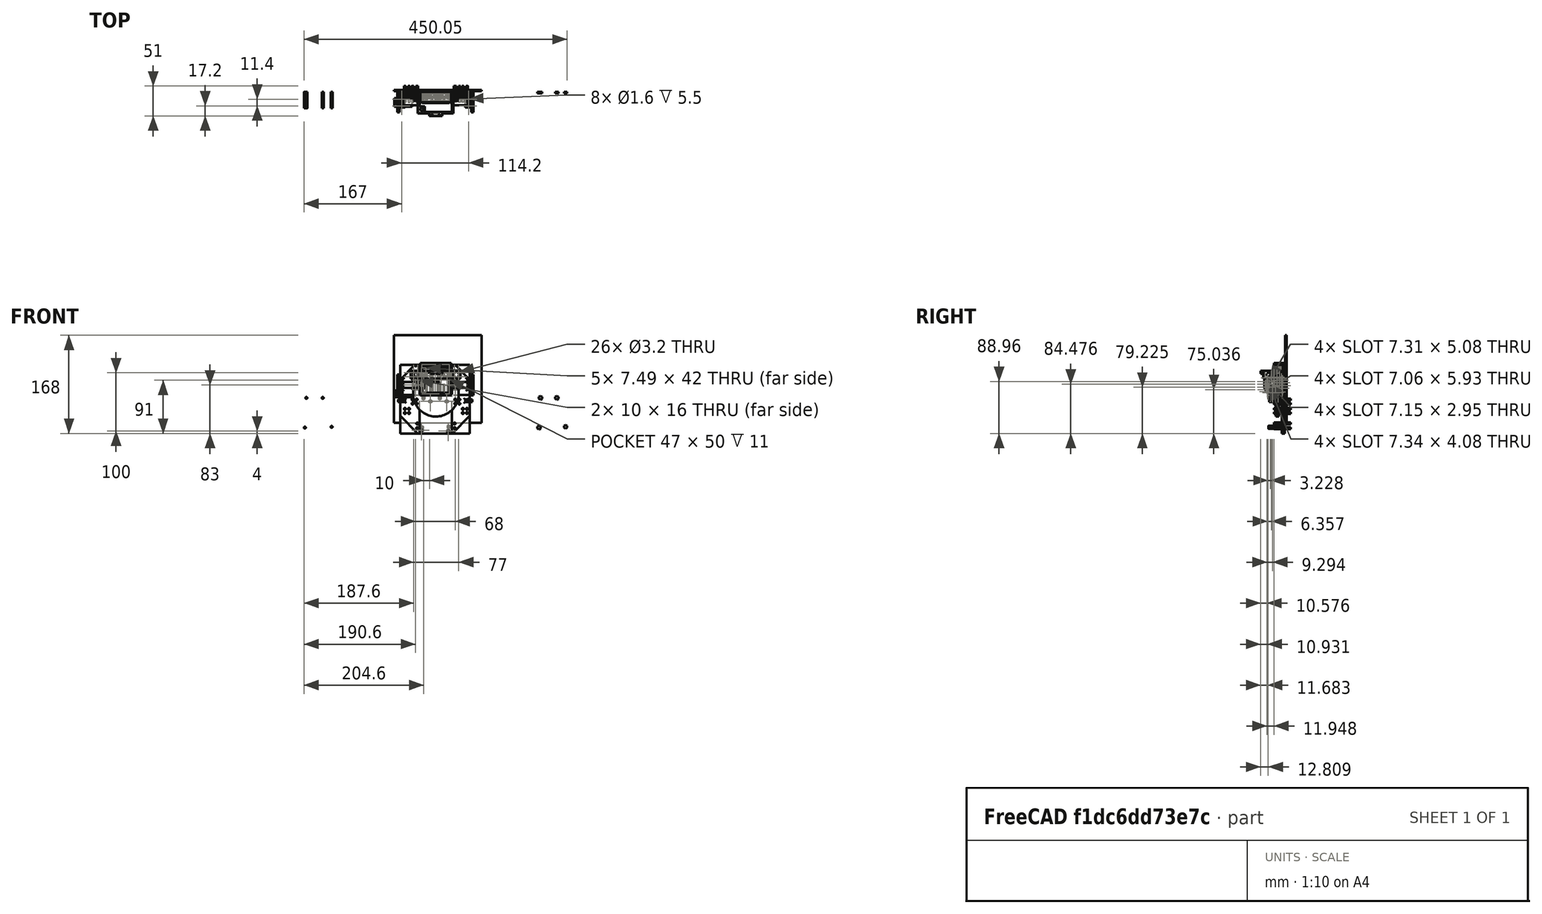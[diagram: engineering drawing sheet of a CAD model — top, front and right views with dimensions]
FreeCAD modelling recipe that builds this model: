
FCSTD DOCUMENT  (FreeCAD 0.16R6712 (Git))
Label: 5028.3 Frank the Robot
License: All rights reserved
LicenseURL: http://en.wikipedia.org/wiki/All_rights_reserved
objects: Part::Cylinder×87, Part::Cut×49, Part::Fuse×46, Part::Box×45, Part::MultiFuse×20, Part::Feature×17, Part::Fillet×10, Part::Mirroring×8, Part::Chamfer×7, Part::Cone×4, Part::Compound×3, Part::Torus×2, App::DocumentObjectGroup×1
note: 298 computed .brp shape members not serialized (recipe doc carries the construction recipe); baked Part::Feature solids carry a one-line shape summary decoded from their .brp

FEATURE [Part::Cylinder] Cylinder
  Angle = 360
  Height = 30
  Radius = 7
FEATURE [Part::Cylinder] Cylinder001
  Angle = 360
  Height = 19
  Placement = pos=(0,0,30) rot=(0,0,1;0rad)
  Radius = 7
FEATURE [Part::Cylinder] Cylinder002
  Angle = 360
  Height = 1.8
  Placement = pos=(0,0,49) rot=(0,0,1;0rad)
  Radius = 2.5
FEATURE [Part::Compound] Compound
  Links = -> [Cylinder,Cylinder002,Cylinder001]
FEATURE [Part::Cylinder] Cylinder003
  Angle = 360
  Height = 30
  Radius = 7
FEATURE [Part::Cylinder] Cylinder004
  Angle = 360
  Height = 19
  Placement = pos=(0,0,30) rot=(0,0,1;0rad)
  Radius = 7
FEATURE [Part::Cylinder] Cylinder005
  Angle = 360
  Height = 1.8
  Placement = pos=(0,0,49) rot=(0,0,1;0rad)
  Radius = 2.5
FEATURE [Part::Compound] Compound001
  Links = -> [Cylinder003,Cylinder005,Cylinder004]
  Placement = pos=(14.5,0,50) rot=(1,0,0;3.14159rad)
FEATURE [Part::Cylinder] Cylinder006
  Angle = 360
  Height = 30
  Radius = 7
FEATURE [Part::Cylinder] Cylinder007
  Angle = 360
  Height = 19
  Placement = pos=(0,0,30) rot=(0,0,1;0rad)
  Radius = 7
FEATURE [Part::Cylinder] Cylinder008
  Angle = 360
  Height = 1.8
  Placement = pos=(0,0,49) rot=(0,0,1;0rad)
  Radius = 2.5
FEATURE [Part::Compound] Compound002
  Links = -> [Cylinder006,Cylinder008,Cylinder007]
  Placement = pos=(29,0,0) rot=(0,0,1;0rad)
FEATURE [Part::Box] Box  label="Cube"
  Height = 50
  Length = 47
  Placement = pos=(-9,-8,0) rot=(0,0,1;0rad)
  Width = 12
FEATURE [Part::Box] Box001  label="Cube001"
  Height = 55
  Length = 53
  Placement = pos=(-12,-8,-2.5) rot=(0,0,1;0rad)
  Width = 11
FEATURE [Part::Cylinder] Cylinder009
  Angle = 360
  Height = 50
  Radius = 7
FEATURE [Part::Cylinder] Cylinder010
  Angle = 360
  Height = 50
  Placement = pos=(14.5,0,0) rot=(0,0,1;0rad)
  Radius = 7
FEATURE [Part::Cut] Cut
  Base = -> Box001
  Tool = -> Box
FEATURE [Part::Box] Box002  label="Cube002"
  Height = 55
  Length = 53
  Placement = pos=(-12,3,-2.5) rot=(0,0,1;0rad)
  Width = 7
FEATURE [Part::Fuse] Fusion
  Base = -> Cut
  Tool = -> Box002
FEATURE [Part::Cut] Cut001  label="No idea why this is here...."
  Base = -> Fusion
  Tool = -> Cylinder009
FEATURE [Part::Cylinder] Cylinder011
  Angle = 360
  Height = 50
  Placement = pos=(29,0,0) rot=(0,0,1;0rad)
  Radius = 7
FEATURE [Part::Box] Box003  label="Cube003"
  Height = 5
  Length = 2
  Placement = pos=(28,-9,-2) rot=(0,0,1;0rad)
  Width = 12
FEATURE [Part::Box] Box004  label="Cube004"
  Height = 5
  Length = 2
  Placement = pos=(18.5,-9,46) rot=(0,0,1;0rad)
  Width = 12
FEATURE [Part::Box] Box005  label="Cube005"
  Height = 5
  Length = 2
  Placement = pos=(-2,-9,46) rot=(0,0,1;0rad)
  Width = 12
FEATURE [Part::Box] Box006  label="Cube006"
  Height = 5
  Length = 3
  Placement = pos=(35,-9,-4) rot=(0,0,1;0rad)
  Width = 12
FEATURE [Part::Cut] Cut008
FEATURE [Part::Torus] Torus001
  Angle1 = -180
  Angle2 = 180
  Angle3 = 360
  Placement = pos=(0,0,2) rot=(0,0,1;0rad)
  Radius1 = 19
  Radius2 = 1.5
FEATURE [Part::Cut] Cut009  label="wheel2"
  Base = -> Cut008
  Placement = pos=(75,-7,15) rot=(0,1,0;1.5708rad)
  Tool = -> Torus001
FEATURE [Part::Torus] Torus
  Angle1 = -180
  Angle2 = 180
  Angle3 = 360
  Placement = pos=(0,0,2) rot=(0,0,1;0rad)
  Radius1 = 19
  Radius2 = 1.5
FEATURE [Part::Cut] Cut010
FEATURE [Part::Cut] Cut011  label="wheel1"
  Base = -> Cut010
  Placement = pos=(-51,-7,15) rot=(0,1,0;1.5708rad)
  Tool = -> Torus
FEATURE [Part::Fuse] Fusion003
FEATURE [Part::Cylinder] Cylinder012
  Angle = 360
  Height = 10
  Placement = pos=(5,-4.5,0) rot=(0,1,0;1.5708rad)
  Radius = 0.8
FEATURE [Part::Fuse] Fusion048  label="right-motor001"
  Base = -> Cylinder012
  Placement = pos=(-51,-7,15) rot=(0,0,1;0rad)
  Tool = -> Fusion003
FEATURE [Part::Fuse] Fusion049
FEATURE [Part::Cylinder] Cylinder013
  Angle = 360
  Height = 10
  Placement = pos=(5,-4.5,0) rot=(0,1,0;1.5708rad)
  Radius = 0.8
FEATURE [Part::Fuse] Fusion050  label="left-motor001"
  Base = -> Cylinder013
  Placement = pos=(79,-7,15) rot=(0,0,1;3.14159rad)
  Tool = -> Fusion049
FEATURE [Part::Box] Box007  label="Cube007"
  Height = 5
  Length = 2
  Placement = pos=(37.5,-9,46) rot=(0,0,1;0rad)
  Width = 12
FEATURE [Part::Box] Box008  label="Cube008"
  Height = 5
  Length = 2
  Placement = pos=(8,-9,-2) rot=(0,0,1;0rad)
  Width = 12
FEATURE [Part::Box] Box009  label="The Ground"
  Height = 150
  Length = 150
  Placement = pos=(-57,11,-50) rot=(0,0,1;0rad)
  Width = 2
FEATURE [Part::Box] Box010  label="Motor Mount Left"
  Height = 16
  Length = 4
  Placement = pos=(69,-13,7) rot=(0,0,1;0rad)
  Width = 20
FEATURE [Part::Box] Box011  label="Motor Mount Right"
  Height = 16
  Length = 4
  Placement = pos=(-46,-13,7) rot=(0,0,1;0rad)
  Width = 20
FEATURE [Part::Box] Box012  label="Motor Support Right"
  Height = 16
  Length = 10
  Placement = pos=(-25,-1,7) rot=(0,0,1;0rad)
  Width = 8
FEATURE [Part::Box] Box013  label="Motor Support Left"
  Height = 16
  Length = 10
  Placement = pos=(43,-1,7) rot=(0,0,1;0rad)
  Width = 8
FEATURE [Part::Cylinder] Cylinder014
  Angle = 360
  Height = 28
  Placement = pos=(40.7,0,-10.3) rot=(1,0,0;1.5708rad)
  Radius = 1.6
FEATURE [Part::Cylinder] Cylinder015
  Angle = 360
  Height = 28
  Placement = pos=(-2.4,0,-59.8) rot=(1,0,0;1.5708rad)
  Radius = 1.6
FEATURE [Part::Cylinder] Cylinder016
  Angle = 360
  Height = 28
  Placement = pos=(-5,0,-9) rot=(1,0,0;1.5708rad)
  Radius = 1.6
FEATURE [Part::Cylinder] Cylinder017
  Angle = 360
  Height = 28
  Placement = pos=(25.5,0,-59.8) rot=(1,0,0;1.5708rad)
  Radius = 1.6
FEATURE [Part::Fuse] Fusion051
  Base = -> Cylinder015
  Tool = -> Cylinder016
FEATURE [Part::Fuse] Fusion052
  Base = -> Cylinder014
  Tool = -> Cylinder017
FEATURE [Part::Fuse] Fusion053  label="Screw holes on Arduino Duo"
  Base = -> Fusion051
  Tool = -> Fusion052
FEATURE [Part::Mirroring] Part__Mirroring  label="XXXXXScrew holes on Arduino Duo (Mirror #1)"
  Base = (0,0,0)
  Normal = (0,0,1)
  Placement = pos=(-204,10,-67) rot=(0,0,1;0rad)
  Source = -> Fusion053
FEATURE [Part::Box] Box014  label="Not used Cube"
  Height = 51
  Length = 119
  Placement = pos=(-46,7,-2) rot=(0,0,1;0rad)
  Width = 3
FEATURE [Part::Box] Box015  label="Cube014 Arduino Support cube"
  Height = 67
  Length = 55
  Placement = pos=(-13,5,-68) rot=(0,0,1;0rad)
  Width = 5
FEATURE [Part::Cylinder] Cylinder018
  Angle = 360
  Height = 5
  Placement = pos=(15,0,0) rot=(1,0,0;1.5708rad)
  Radius = 39
FEATURE [Part::Cut] Cut014  label="M3 Nut"
  Base = -> Cut001
  Placement = pos=(-6.4,10,-7.2) rot=(1,0,0;1.5708rad)
  Tool = -> Cylinder001
FEATURE [Part::Cut] Cut015  label="M3 Nut001"
  Base = -> Cut001
  Placement = pos=(21.5,10,-7.2) rot=(1,0,0;1.5708rad)
  Tool = -> Cylinder001
FEATURE [Part::Cut] Cut016  label="M3 Nut002"
  Base = -> Cut001
  Placement = pos=(36.7,10,-56.7) rot=(1,0,0;1.5708rad)
  Tool = -> Cylinder001
FEATURE [Part::Cut] Cut017  label="M3 Nut003"
  Base = -> Cut001
  Placement = pos=(-9,10,-58) rot=(1,0,0;1.5708rad)
  Tool = -> Cylinder001
FEATURE [Part::Cut] Cut018
  Base = -> Cut
  Placement = pos=(-9,10,-58) rot=(1,0,0;1.5708rad)
  Tool = -> Box006
FEATURE [Part::Cut] Cut019
  Base = -> Cut
  Placement = pos=(36.7,10,-56.7) rot=(1,0,0;1.5708rad)
  Tool = -> Box006
FEATURE [Part::Cut] Cut020
  Base = -> Cut
  Placement = pos=(-6.4,10,-7.2) rot=(1,0,0;1.5708rad)
  Tool = -> Box006
FEATURE [Part::Cut] Cut021
  Base = -> Cut
  Placement = pos=(21.5,10,-7.2) rot=(1,0,0;1.5708rad)
  Tool = -> Box006
FEATURE [Part::MultiFuse] Fusion054  label="XXXXXHex Holes"
  Placement = pos=(200,0,0) rot=(0,0,1;0rad)
  Shapes = -> [Cut018,Cut021,Cut019,Cut020]
FEATURE [Part::Box] Box016  label="Cube015"
  Height = 117
  Length = 33
  Placement = pos=(-46,7,-68) rot=(0,0,1;0rad)
  Width = 3
FEATURE [Part::Box] Box017  label="Cube016"
  Height = 117
  Length = 31
  Placement = pos=(42,7,-68) rot=(0,0,1;0rad)
  Width = 3
FEATURE [Part::Cylinder] Cylinder019
  Angle = 360
  Height = 28
  Placement = pos=(48,20,-10) rot=(1,0,0;1.5708rad)
  Radius = 1.6
FEATURE [Part::Cylinder] Cylinder020
  Angle = 360
  Height = 28
  Placement = pos=(47,20,-51) rot=(1,0,0;1.5708rad)
  Radius = 1.6
FEATURE [Part::Cylinder] Cylinder021
  Angle = 360
  Height = 28
  Placement = pos=(48,20,-17) rot=(1,0,0;1.5708rad)
  Radius = 1.6
FEATURE [Part::Cylinder] Cylinder022
  Angle = 360
  Height = 28
  Placement = pos=(47,20,-59) rot=(1,0,0;1.5708rad)
  Radius = 1.6
FEATURE [Part::Cylinder] Cylinder023
  Angle = 360
  Height = 28
  Placement = pos=(55,20,-17) rot=(1,0,0;1.5708rad)
  Radius = 1.6
FEATURE [Part::Cylinder] Cylinder024
  Angle = 360
  Height = 28
  Placement = pos=(55,20,-10) rot=(1,0,0;1.5708rad)
  Radius = 1.6
FEATURE [Part::MultiFuse] Fusion055
  Shapes = -> [Cylinder021,Cylinder023,Cylinder024,Cylinder019]
FEATURE [Part::MultiFuse] Fusion056
  Placement = pos=(13,0,-16) rot=(0,0,1;0rad)
  Shapes = -> [Cylinder021,Cylinder023,Cylinder024,Cylinder019]
FEATURE [Part::MultiFuse] Fusion057  label="Mount holes top left"
  Placement = pos=(-1,0,46) rot=(0,0,1;0rad)
  Shapes = -> [Cylinder021,Cylinder023,Cylinder024,Cylinder019]
FEATURE [Part::MultiFuse] Fusion058  label="Mount holes top right"
  Placement = pos=(-71,0,46) rot=(0,0,1;0rad)
  Shapes = -> [Cylinder021,Cylinder023,Cylinder024,Cylinder019]
FEATURE [Part::MultiFuse] Fusion059
  Shapes = -> [Cylinder022,Cylinder020,Fusion055,Fusion056]
FEATURE [Part::Mirroring] Part__Mirroring001  label="Mount holes bottom right"
  Base = (0,0,0)
  Normal = (1,0,0)
  Placement = pos=(30,0,0) rot=(0,0,1;0rad)
  Source = -> Fusion059
FEATURE [Part::Cylinder] Cylinder025
  Angle = 360
  Height = 28
  Placement = pos=(48,20,-10) rot=(1,0,0;1.5708rad)
  Radius = 1.6
FEATURE [Part::Cylinder] Cylinder026
  Angle = 360
  Height = 28
  Placement = pos=(47,20,-51) rot=(1,0,0;1.5708rad)
  Radius = 1.6
FEATURE [Part::Cylinder] Cylinder027
  Angle = 360
  Height = 28
  Placement = pos=(48,20,-17) rot=(1,0,0;1.5708rad)
  Radius = 1.6
FEATURE [Part::Cylinder] Cylinder028
  Angle = 360
  Height = 28
  Placement = pos=(47,20,-59) rot=(1,0,0;1.5708rad)
  Radius = 1.6
FEATURE [Part::Cylinder] Cylinder029
  Angle = 360
  Height = 28
  Placement = pos=(55,20,-17) rot=(1,0,0;1.5708rad)
  Radius = 1.6
FEATURE [Part::Cylinder] Cylinder030
  Angle = 360
  Height = 28
  Placement = pos=(55,20,-10) rot=(1,0,0;1.5708rad)
  Radius = 1.6
FEATURE [Part::MultiFuse] Fusion060
  Shapes = -> [Cylinder027,Cylinder029,Cylinder030,Cylinder025]
FEATURE [Part::MultiFuse] Fusion061
  Placement = pos=(13,0,-16) rot=(0,0,1;0rad)
  Shapes = -> [Cylinder027,Cylinder029,Cylinder030,Cylinder025]
FEATURE [Part::MultiFuse] Fusion062  label="Mount holes bottom left"
  Shapes = -> [Cylinder028,Cylinder026,Fusion060,Fusion061]
FEATURE [Part::Cylinder] Cylinder031  label="Cylinder087"
  Angle = 360
  Height = 10
  Placement = pos=(0,18,29) rot=(0,0,1;0rad)
  Radius = 2.25
FEATURE [Part::Cylinder] Cylinder032  label="Cylinder088"
  Angle = 360
  Height = 10
  Placement = pos=(4.5,18,32) rot=(0,0,1;0rad)
  Radius = 1
FEATURE [Part::Cylinder] Cylinder033  label="Cylinder089"
  Angle = 360
  Height = 10
  Placement = pos=(-4.5,18,32) rot=(0,0,1;0rad)
  Radius = 1
FEATURE [Part::Fuse] Fusion009  label="Mounting Screw Holes"
  Base = -> Cylinder032
  Tool = -> Cylinder033
FEATURE [Part::Fuse] Fusion071  label="Motor Holes Left"
  Base = -> Cylinder031
  Placement = pos=(37,-7,-3) rot=(0.57735,0.57735,0.57735;2.0944rad)
  Tool = -> Fusion009
FEATURE [Part::Cylinder] Cylinder034  label="Cylinder090"
  Angle = 360
  Height = 10
  Placement = pos=(0,18,29) rot=(0,0,1;0rad)
  Radius = 2.25
FEATURE [Part::Cylinder] Cylinder035  label="Cylinder091"
  Angle = 360
  Height = 10
  Placement = pos=(4.5,18,32) rot=(0,0,1;0rad)
  Radius = 1
FEATURE [Part::Cylinder] Cylinder036  label="Cylinder092"
  Angle = 360
  Height = 10
  Placement = pos=(-4.5,18,32) rot=(0,0,1;0rad)
  Radius = 1
FEATURE [Part::Fuse] Fusion072  label="Mounting Screw Holes001"
  Base = -> Cylinder035
  Tool = -> Cylinder036
FEATURE [Part::Fuse] Fusion073  label="Motor Holes Right"
  Base = -> Cylinder034
  Placement = pos=(-79,-7,-3) rot=(0.57735,0.57735,0.57735;2.0944rad)
  Tool = -> Fusion072
FEATURE [Part::Cylinder] Cylinder037  label="Cylinder093"
  Angle = 360
  Height = 28
  Placement = pos=(40.7,0,-10.3) rot=(1,0,0;1.5708rad)
  Radius = 1.6
FEATURE [Part::Cylinder] Cylinder038  label="Cylinder094"
  Angle = 360
  Height = 28
  Placement = pos=(-2.4,0,-59.8) rot=(1,0,0;1.5708rad)
  Radius = 1.6
FEATURE [Part::Cylinder] Cylinder039  label="Cylinder095"
  Angle = 360
  Height = 28
  Placement = pos=(-5,0,-9) rot=(1,0,0;1.5708rad)
  Radius = 1.6
FEATURE [Part::Cylinder] Cylinder040  label="Cylinder096"
  Angle = 360
  Height = 28
  Placement = pos=(25.5,0,-59.8) rot=(1,0,0;1.5708rad)
  Radius = 1.6
FEATURE [Part::Fuse] Fusion074
  Base = -> Cylinder038
  Tool = -> Cylinder039
FEATURE [Part::Fuse] Fusion075
  Base = -> Cylinder037
  Tool = -> Cylinder040
FEATURE [Part::Fuse] Fusion076  label="Screw holes on Arduino Duo001"
  Base = -> Fusion074
  Tool = -> Fusion075
FEATURE [Part::Mirroring] Part__Mirroring002  label="Screw holes on Arduino Duo (Mirror #1)001"
  Base = (0,0,0)
  Normal = (0,0,1)
  Placement = pos=(-4,10,-67) rot=(0,0,1;0rad)
  Source = -> Fusion076
FEATURE [Part::Mirroring] Part__Mirroring003  label="Screw holes on Arduino Duo (Mirror #1)001 (Mirror #4)"
  Base = (0,0,0)
  Normal = (1,0,0)
  Placement = pos=(27,0,-6) rot=(0,0,1;0rad)
  Source = -> Part__Mirroring002
FEATURE [Part::Box] Box018  label="Cube017"
  Height = 50
  Length = 47
  Placement = pos=(-9,-8,0) rot=(0,0,1;0rad)
  Width = 12
FEATURE [Part::Box] Box019  label="Cube018"
  Height = 55
  Length = 53
  Placement = pos=(-12,-8,-2.5) rot=(0,0,1;0rad)
  Width = 11
FEATURE [Part::Cut] Cut031
  Base = -> Box019
  Tool = -> Box018
FEATURE [Part::Box] Box020  label="Cube019"
  Height = 5
  Length = 3
  Placement = pos=(35,-9,-4) rot=(0,0,1;0rad)
  Width = 12
FEATURE [Part::Cut] Cut032
  Base = -> Cut031
  Placement = pos=(-9,10,-58) rot=(1,0,0;1.5708rad)
  Tool = -> Box020
FEATURE [Part::Cut] Cut033
  Base = -> Cut031
  Placement = pos=(36.7,10,-56.7) rot=(1,0,0;1.5708rad)
  Tool = -> Box020
FEATURE [Part::Cut] Cut034
  Base = -> Cut031
  Placement = pos=(-6.4,10,-7.2) rot=(1,0,0;1.5708rad)
  Tool = -> Box020
FEATURE [Part::Cut] Cut035
  Base = -> Cut031
  Placement = pos=(21.5,10,-7.2) rot=(1,0,0;1.5708rad)
  Tool = -> Box020
FEATURE [Part::MultiFuse] Fusion077
  Shapes = -> [Cut032,Cut035,Cut033,Cut034]
FEATURE [Part::Mirroring] Part__Mirroring004  label="Hex Holes"
  Base = (0,0,0)
  Normal = (1,0,0)
  Placement = pos=(27,0,-6) rot=(0,0,1;0rad)
  Source = -> Fusion077
FEATURE [Part::Box] Box021  label="Cube020"
  Height = 13
  Length = 61
  Placement = pos=(-16,-27,26) rot=(0,0,1;0rad)
  Width = 34
FEATURE [Part::Box] Box022  label="Cube021"
  Height = 13
  Length = 12
  Placement = pos=(45,4,26) rot=(0,0,1;0rad)
  Width = 3
FEATURE [Part::Box] Box023  label="Cube022"
  Height = 13
  Length = 12
  Placement = pos=(-28,4,26) rot=(0,0,1;0rad)
  Width = 3
FEATURE [Part::Box] Box024  label="Cube023"
  Height = 13
  Length = 55
  Placement = pos=(-13,-24,26) rot=(0,0,1;0rad)
  Width = 31
FEATURE [Part::Cylinder] Cylinder041  label="Cylinder097"
  Angle = 360
  Height = 28
  Placement = pos=(54,20,29) rot=(1,0,0;1.5708rad)
  Radius = 1.6
FEATURE [Part::Cylinder] Cylinder042  label="Cylinder098"
  Angle = 360
  Height = 28
  Placement = pos=(54,20,36) rot=(1,0,0;1.5708rad)
  Radius = 1.6
FEATURE [Part::Cylinder] Cylinder043  label="Cylinder099"
  Angle = 360
  Height = 28
  Placement = pos=(-23,20,29) rot=(1,0,0;1.5708rad)
  Radius = 1.6
FEATURE [Part::Cylinder] Cylinder044  label="Cylinder100"
  Angle = 360
  Height = 28
  Placement = pos=(-23,20,36) rot=(1,0,0;1.5708rad)
  Radius = 1.6
FEATURE [Part::Cylinder] Cylinder045  label="Cylinder101"
  Angle = 360
  Height = 10
  Placement = pos=(36,-17.25,32.5) rot=(0,1,0;1.5708rad)
  Radius = 3.25
FEATURE [Part::Cut] Cut037
  Base = -> Box021
  Tool = -> Box024
FEATURE [Part::Cut] Cut038
  Base = -> Cut037
  Tool = -> Cylinder045
FEATURE [Part::Box] Box025  label="Cube024"
  Height = 5
  Length = 22
  Placement = pos=(3.5,-31,34) rot=(0,0,1;0rad)
  Width = 4
FEATURE [Part::Cylinder] Cylinder046  label="Cylinder102"
  Angle = 360
  Height = 10
  Placement = pos=(20.65,-29,30) rot=(0,0,1;0rad)
  Radius = 0.85
FEATURE [Part::Cylinder] Cylinder047  label="Cylinder103"
  Angle = 360
  Height = 10
  Placement = pos=(8.35,-29,40) rot=(1,0,0;3.14159rad)
  Radius = 0.85
FEATURE [Part::Fuse] Fusion078
  Base = -> Cylinder046
  Tool = -> Cylinder047
FEATURE [Part::Cut] Cut039
  Base = -> Box025
  Tool = -> Fusion078
FEATURE [Part::Fuse] Fusion079
  Base = -> Cut038
  Tool = -> Cut039
FEATURE [Part::Fuse] Fusion080
  Base = -> Cylinder043
  Tool = -> Cylinder044
FEATURE [Part::Fuse] Fusion081
  Base = -> Cylinder041
  Tool = -> Cylinder042
FEATURE [Part::Fuse] Fusion082
  Base = -> Box023
  Tool = -> Fusion079
FEATURE [Part::Fuse] Fusion083
  Base = -> Box022
  Tool = -> Fusion082
FEATURE [Part::Cut] Cut040
  Base = -> Fusion083
  Tool = -> Fusion081
FEATURE [Part::Cut] Cut041  label="Switch Bracket"
  Base = -> Cut040
  Tool = -> Fusion080
FEATURE [Part::Cylinder] Cylinder048  label="Cylinder104"
  Angle = 360
  Height = 28
  Placement = pos=(-23,20,29) rot=(1,0,0;1.5708rad)
  Radius = 1.6
FEATURE [Part::Cylinder] Cylinder049  label="Cylinder105"
  Angle = 360
  Height = 28
  Placement = pos=(-23,20,36) rot=(1,0,0;1.5708rad)
  Radius = 1.6
FEATURE [Part::Fuse] Fusion084
  Base = -> Cylinder048
  Placement = pos=(1,0,0) rot=(0,0,1;0rad)
  Tool = -> Cylinder049
FEATURE [Part::Cylinder] Cylinder050  label="Cylinder106"
  Angle = 360
  Height = 28
  Placement = pos=(-23,20,29) rot=(1,0,0;1.5708rad)
  Radius = 1.6
FEATURE [Part::Cylinder] Cylinder051  label="Cylinder107"
  Angle = 360
  Height = 28
  Placement = pos=(-23,20,36) rot=(1,0,0;1.5708rad)
  Radius = 1.6
FEATURE [Part::Fuse] Fusion085
  Base = -> Cylinder050
  Placement = pos=(-1,0,0) rot=(0,0,1;0rad)
  Tool = -> Cylinder051
FEATURE [Part::Cut] Cut042
  Base = -> Cut041
  Tool = -> Fusion084
FEATURE [Part::Cut] Cut043  label="Switch Bracket001"
  Base = -> Cut042
  Tool = -> Fusion085
FEATURE [Part::Cylinder] Cylinder052  label="Cylinder108"
  Angle = 360
  Height = 42
  Radius = 4.8
FEATURE [Part::Cylinder] Cylinder053  label="Cylinder109"
  Angle = 360
  Height = 1.6
  Placement = pos=(0,0,42) rot=(0,0,1;0rad)
  Radius = 1.65
FEATURE [Part::Fuse] Fusion086
  Base = -> Cylinder052
  Placement = pos=(2,0,0) rot=(0,0,1;0rad)
  Tool = -> Cylinder053
FEATURE [Part::Cylinder] Cylinder054  label="Cylinder110"
  Angle = 360
  Height = 42
  Radius = 4.8
FEATURE [Part::Cylinder] Cylinder055  label="Cylinder111"
  Angle = 360
  Height = 1.6
  Placement = pos=(0,0,42) rot=(0,0,1;0rad)
  Radius = 1.65
FEATURE [Part::Fuse] Fusion087
  Base = -> Cylinder054
  Placement = pos=(12,0,0) rot=(0,0,1;0rad)
  Tool = -> Cylinder055
FEATURE [Part::Cylinder] Cylinder056  label="Cylinder112"
  Angle = 360
  Height = 42
  Radius = 4.8
FEATURE [Part::Cylinder] Cylinder057  label="Cylinder113"
  Angle = 360
  Height = 1.6
  Placement = pos=(0,0,42) rot=(0,0,1;0rad)
  Radius = 1.65
FEATURE [Part::Fuse] Fusion088
  Base = -> Cylinder056
  Placement = pos=(22,0,0) rot=(0,0,1;0rad)
  Tool = -> Cylinder057
FEATURE [Part::Cylinder] Cylinder058  label="Cylinder114"
  Angle = 360
  Height = 42
  Radius = 4.8
FEATURE [Part::Cylinder] Cylinder059  label="Cylinder115"
  Angle = 360
  Height = 1.6
  Placement = pos=(0,0,42) rot=(0,0,1;0rad)
  Radius = 1.65
FEATURE [Part::Fuse] Fusion089
  Base = -> Cylinder058
  Placement = pos=(32,0,0) rot=(0,0,1;0rad)
  Tool = -> Cylinder059
FEATURE [Part::Cylinder] Cylinder060  label="Cylinder116"
  Angle = 360
  Height = 42
  Radius = 4.8
FEATURE [Part::Cylinder] Cylinder061  label="Cylinder117"
  Angle = 360
  Height = 1.6
  Placement = pos=(0,0,42) rot=(0,0,1;0rad)
  Radius = 1.65
FEATURE [Part::Fuse] Fusion093
  Base = -> Cylinder060
  Placement = pos=(-8,0,0) rot=(0,0,1;0rad)
  Tool = -> Cylinder061
FEATURE [Part::MultiFuse] Fusion094  label="AAA Batts"
  Placement = pos=(2.5,0,2) rot=(0,0,1;0rad)
  Shapes = -> [Fusion093,Fusion086,Fusion087,Fusion088,Fusion089]
FEATURE [Part::Cylinder] Cylinder062  label="Cylinder118"
  Angle = 360
  Height = 10
  Radius = 17
FEATURE [Part::Cylinder] Cylinder063  label="Cylinder119"
  Angle = 360
  Height = 16
  Placement = pos=(0,0,-4) rot=(0,0,1;0rad)
  Radius = 10
FEATURE [Part::Cut] Cut044
  Base = -> Cylinder062
  Tool = -> Cylinder063
FEATURE [Part::Box] Box026  label="Cube025"
  Height = 20
  Length = 18
  Placement = pos=(0,0,-5) rot=(0,0,1;0rad)
  Width = 20
FEATURE [Part::Box] Box027  label="Cube026"
  Height = 20
  Length = 10
  Placement = pos=(0,0,-5) rot=(0,0,1;0.174533rad)
  Width = 20
FEATURE [Part::Cut] Cut045
  Base = -> Box027
  Tool = -> Box026
FEATURE [Part::Feature] Cut045001
  Placement = pos=(0,0,0) rot=(0,0,1;0.349066rad)
  shape: bbox 10 x 22.32 x 20 mm, 7 faces (baked)
FEATURE [Part::Feature] Cut045002
  Placement = pos=(0,0,0) rot=(0,0,1;0.698132rad)
  shape: bbox 15.32 x 20.52 x 20 mm, 7 faces (baked)
FEATURE [Part::Feature] Cut045003
  Placement = pos=(0,0,0) rot=(0,0,1;1.0472rad)
  shape: bbox 18.79 x 16.24 x 20 mm, 7 faces (baked)
FEATURE [Part::Feature] Cut045004
  Placement = pos=(0,0,0) rot=(0,0,1;1.39626rad)
  shape: bbox 20 x 10 x 20 mm, 7 faces (baked)
FEATURE [Part::Feature] Cut045005
  Placement = pos=(0,0,0) rot=(0,0,1;1.74533rad)
  shape: bbox 22.21 x 9.894 x 20 mm, 7 faces (baked)
FEATURE [Part::Feature] Cut045006
  Placement = pos=(0,0,0) rot=(0,0,1;2.0944rad)
  shape: bbox 21.75 x 12.86 x 20 mm, 7 faces (baked)
FEATURE [Part::Feature] Cut045007
  Placement = pos=(0,0,0) rot=(0,0,1;2.44346rad)
  shape: bbox 18.66 x 17.32 x 20 mm, 7 faces (baked)
FEATURE [Part::Feature] Cut045008
  Placement = pos=(0,0,0) rot=(0,0,1;2.79253rad)
  shape: bbox 13.32 x 19.7 x 20 mm, 7 faces (baked)
FEATURE [Part::Feature] Cut045009
  Placement = pos=(0,0,0) rot=(0,0,1;3.14159rad)
  shape: bbox 10.1 x 21.43 x 20 mm, 7 faces (baked)
FEATURE [Part::Feature] Cut045010
  Placement = pos=(0,0,0) rot=(0,0,1;3.49066rad)
  shape: bbox 10 x 22.32 x 20 mm, 7 faces (baked)
FEATURE [Part::Feature] Cut045011
  Placement = pos=(0,0,0) rot=(0,0,1;3.83972rad)
  shape: bbox 15.32 x 20.52 x 20 mm, 7 faces (baked)
FEATURE [Part::Feature] Cut045012
  Placement = pos=(0,0,0) rot=(0,0,1;4.18879rad)
  shape: bbox 18.79 x 16.24 x 20 mm, 7 faces (baked)
FEATURE [Part::Feature] Cut045013
  Placement = pos=(0,0,0) rot=(0,0,-1;1.74533rad)
  shape: bbox 20 x 10 x 20 mm, 7 faces (baked)
FEATURE [Part::Feature] Cut045014
  Placement = pos=(0,0,0) rot=(0,0,-1;1.39626rad)
  shape: bbox 22.21 x 9.894 x 20 mm, 7 faces (baked)
FEATURE [Part::Feature] Cut045015
  Placement = pos=(0,0,0) rot=(0,0,-1;1.0472rad)
  shape: bbox 21.75 x 12.86 x 20 mm, 7 faces (baked)
FEATURE [Part::Feature] Cut045016
  Placement = pos=(0,0,0) rot=(0,0,-1;0.698132rad)
  shape: bbox 18.66 x 17.32 x 20 mm, 7 faces (baked)
FEATURE [Part::Feature] Cut045017
  Placement = pos=(0,0,0) rot=(0,0,-1;0.349066rad)
  shape: bbox 13.32 x 19.7 x 20 mm, 7 faces (baked)
FEATURE [Part::MultiFuse] Fusion095
  Shapes = -> [Cut045001,Cut045008,Cut045010,Cut045009,Cut045005,Cut045003,Cut045006,Cut045002,Cut045004,Cut045007,Cut045016,Cut045017,Cut045011,Cut045012,Cut045013,Cut045014,Cut045015,Cut045]
FEATURE [Part::Cut] Cut045018
  Base = -> Cut044
  Placement = pos=(72,-7,15) rot=(0,1,0;1.5708rad)
  Tool = -> Fusion095
FEATURE [Part::Cut] Cut045019  label="Wheel with Spokes AB"
  Base = -> Cut009
  Tool = -> Cut045018
FEATURE [Part::Box] Box028  label="Cube027"
  Height = 5
  Length = 2
  Placement = pos=(37.5,-9,-2) rot=(0,0,1;0rad)
  Width = 12
FEATURE [Part::Box] Box029  label="Cube028"
  Height = 50
  Length = 47
  Placement = pos=(-9,-8,0) rot=(0,0,1;0rad)
  Width = 12
FEATURE [Part::Box] Box030  label="Cube029"
  Height = 55
  Length = 53
  Placement = pos=(-12,-8,-2.5) rot=(0,0,1;0rad)
  Width = 11
FEATURE [Part::Cylinder] Cylinder064  label="Cylinder120"
  Angle = 360
  Height = 50
  Radius = 7
FEATURE [Part::Cut] Cut045020
  Base = -> Box030
  Tool = -> Box029
FEATURE [Part::Box] Box031  label="Cube030"
  Height = 55
  Length = 53
  Placement = pos=(-12,3,-2.5) rot=(0,0,1;0rad)
  Width = 7
FEATURE [Part::Fuse] Fusion096
  Base = -> Cut045020
  Tool = -> Box031
FEATURE [App::DocumentObjectGroup] Group  label="Older version parts"
  Group = -> [Compound,Compound001,Compound002,Cylinder064,Cylinder010,Cylinder011,Fusion096,Part__Mirroring,Fusion054,Part__Mirroring001,Fusion062]
FEATURE [Part::Box] Box032  label="Battery Base"
  Height = 50
  Length = 55
  Placement = pos=(-13,3,-1) rot=(0,0,1;0rad)
  Width = 7
FEATURE [Part::Box] Box033  label="Cube031"
  Height = 30
  Length = 10
  Placement = pos=(-14,-25,9) rot=(0,0,1;0rad)
  Width = 10
FEATURE [Part::Cylinder] Cylinder065  label="Cylinder121"
  Angle = 360
  Height = 42
  Radius = 4.8
FEATURE [Part::Cylinder] Cylinder066  label="Cylinder122"
  Angle = 360
  Height = 1.6
  Placement = pos=(0,0,42) rot=(0,0,1;0rad)
  Radius = 1.65
FEATURE [Part::Fuse] Fusion097
  Base = -> Cylinder065
  Placement = pos=(2,0,0) rot=(0,0,1;0rad)
  Tool = -> Cylinder066
FEATURE [Part::Cylinder] Cylinder067  label="Cylinder123"
  Angle = 360
  Height = 42
  Radius = 4.8
FEATURE [Part::Cylinder] Cylinder068  label="Cylinder124"
  Angle = 360
  Height = 1.6
  Placement = pos=(0,0,42) rot=(0,0,1;0rad)
  Radius = 1.65
FEATURE [Part::Fuse] Fusion098
  Base = -> Cylinder067
  Placement = pos=(12,0,0) rot=(0,0,1;0rad)
  Tool = -> Cylinder068
FEATURE [Part::Cylinder] Cylinder069  label="Cylinder125"
  Angle = 360
  Height = 42
  Radius = 4.8
FEATURE [Part::Cylinder] Cylinder070  label="Cylinder126"
  Angle = 360
  Height = 1.6
  Placement = pos=(0,0,42) rot=(0,0,1;0rad)
  Radius = 1.65
FEATURE [Part::Fuse] Fusion099
  Base = -> Cylinder069
  Placement = pos=(22,0,0) rot=(0,0,1;0rad)
  Tool = -> Cylinder070
FEATURE [Part::Cylinder] Cylinder071  label="Cylinder127"
  Angle = 360
  Height = 42
  Radius = 4.8
FEATURE [Part::Cylinder] Cylinder072  label="Cylinder128"
  Angle = 360
  Height = 1.6
  Placement = pos=(0,0,42) rot=(0,0,1;0rad)
  Radius = 1.65
FEATURE [Part::Fuse] Fusion100
  Base = -> Cylinder071
  Placement = pos=(32,0,0) rot=(0,0,1;0rad)
  Tool = -> Cylinder072
FEATURE [Part::Cylinder] Cylinder073  label="Cylinder129"
  Angle = 360
  Height = 42
  Radius = 4.8
FEATURE [Part::Cylinder] Cylinder074  label="Cylinder130"
  Angle = 360
  Height = 1.6
  Placement = pos=(0,0,42) rot=(0,0,1;0rad)
  Radius = 1.65
FEATURE [Part::Fuse] Fusion101
  Base = -> Cylinder073
  Placement = pos=(-8,0,0) rot=(0,0,1;0rad)
  Tool = -> Cylinder074
FEATURE [Part::MultiFuse] Fusion102  label="AAA Batts001"
  Placement = pos=(2,0,2) rot=(0,0,1;0rad)
  Shapes = -> [Fusion101,Fusion097,Fusion098,Fusion099,Fusion100]
FEATURE [Part::Cylinder] Cylinder075  label="Cylinder131"
  Angle = 360
  Height = 10
  Placement = pos=(-9,-20,4) rot=(0,0,1;0rad)
  Radius = 3.1
FEATURE [Part::Cylinder] Cylinder076  label="Cylinder132"
  Angle = 360
  Height = 27
  Placement = pos=(-9,-20,14) rot=(0,0,1;0rad)
  Radius = 2.6
FEATURE [Part::Fuse] Fusion103  label="phototransistor hole"
  Base = -> Cylinder075
  Tool = -> Cylinder076
FEATURE [Part::Cut] Cut045021
  Base = -> Box033
  Tool = -> Fusion103
FEATURE [Part::Fuse] Fusion104  label="Switch Mount with phototransistor hole"
  Base = -> Cut043
  Tool = -> Cut045021
FEATURE [Part::Cut] Cut045022
  Base = -> Box032
  Tool = -> Fusion102
FEATURE [Part::Box] Box034  label="Cube032"
  Height = 2.5
  Length = 55
  Placement = pos=(-13,-9,-1) rot=(0,0,1;0rad)
  Width = 12
FEATURE [Part::Box] Box035  label="Cube033"
  Height = 2.5
  Length = 55
  Placement = pos=(-13,-9,46.5) rot=(0,0,1;0rad)
  Width = 12
FEATURE [Part::Box] Box036  label="Cube034"
  Height = 50
  Length = 2.5
  Placement = pos=(-13,-9,-1) rot=(0,0,1;0rad)
  Width = 12
FEATURE [Part::Box] Box037  label="Cube035"
  Height = 50
  Length = 2.5
  Placement = pos=(39.5,-9,-1) rot=(0,0,1;0rad)
  Width = 12
FEATURE [Part::MultiFuse] Fusion105
  Shapes = -> [Box034,Box036,Box037,Box035]
FEATURE [Part::Box] Box038  label="Cube036"
  Height = 5
  Length = 2
  Placement = pos=(-10.5,-9,46) rot=(0,0,1;0rad)
  Width = 12
FEATURE [Part::Box] Box039  label="Cube037"
  Height = 5
  Length = 2
  Placement = pos=(-10.5,-9,-2) rot=(0,0,1;0rad)
  Width = 12
FEATURE [Part::MultiFuse] Fusion106
  Shapes = -> [Box039,Box038,Box028,Box007]
FEATURE [Part::MultiFuse] Fusion107
  Shapes = -> [Box003,Box004,Box005,Box008]
FEATURE [Part::Cut] Cut045023
  Base = -> Fusion105
  Tool = -> Fusion106
FEATURE [Part::Cut] Cut045024
  Base = -> Cut045023
  Tool = -> Fusion107
FEATURE [Part::Box] Box040  label="Cube038"
  Height = 1.6
  Length = 30
  Placement = pos=(-56,-15.5,-6) rot=(0,0,1;0rad)
  Width = 15
FEATURE [Part::Box] Box041  label="Cube039"
  Height = 10
  Length = 14
  Placement = pos=(-56,-10.5,-4.5) rot=(0,0,1;0rad)
  Width = 6
FEATURE [Part::Box] Box042  label="Cube040"
  Height = 10
  Length = 5.3
  Placement = pos=(-51.7,-11.5,-4.5) rot=(0,0,1;0rad)
  Width = 8
FEATURE [Part::Cut] Cut045025
  Base = -> Box041
  Tool = -> Box042
FEATURE [Part::Fuse] Fusion108  label="Spoke Sensor PCB"
  Base = -> Box040
  Tool = -> Cut045025
FEATURE [Part::Cylinder] Cylinder077  label="Cylinder133"
  Angle = 360
  Height = 14.5
  Placement = pos=(-43.6,-2.4,-9) rot=(0,0,1;0rad)
  Radius = 0.8
FEATURE [Part::Cylinder] Cylinder078  label="Cylinder134"
  Angle = 360
  Height = 14.5
  Placement = pos=(-43.6,-13.8,-9) rot=(0,0,1;0rad)
  Radius = 0.8
FEATURE [Part::Fuse] Fusion109
  Base = -> Cylinder077
  Tool = -> Cylinder078
FEATURE [Part::Cut] Cut045026  label="Spoke Sensor PCB001"
  Base = -> Fusion108
  Tool = -> Fusion109
FEATURE [Part::Cylinder] Cylinder079  label="Cylinder135"
  Angle = 360
  Height = 14.5
  Placement = pos=(-43.6,-2.4,-15) rot=(0,0,1;0rad)
  Radius = 0.8
FEATURE [Part::Cylinder] Cylinder080  label="Cylinder136"
  Angle = 360
  Height = 14.5
  Placement = pos=(-43.6,-13.8,-15) rot=(0,0,1;0rad)
  Radius = 0.8
FEATURE [Part::Fuse] Fusion110
  Base = -> Cut045022
  Tool = -> Cut045024
FEATURE [Part::Box] Box043  label="Cube041"
  Height = 4
  Length = 12
  Placement = pos=(-50,-16.75,-14) rot=(0,0,1;0rad)
  Width = 26.75
FEATURE [Part::Chamfer] Chamfer
  Base = -> Box043
  Edges = 1 edges r=7: [Edge3]
FEATURE [Part::Cone] Cone
  Angle = 360
  Height = 1.5
  Placement = pos=(-43.6,-2.4,-10) rot=(0,0,1;0rad)
  Radius1 = 2.75
  Radius2 = 1.25
FEATURE [Part::Cone] Cone001
  Angle = 360
  Height = 1.5
  Placement = pos=(-43.6,-13.8,-10) rot=(0,0,1;0rad)
  Radius1 = 2.75
  Radius2 = 1.25
FEATURE [Part::Fuse] Fusion111
  Base = -> Cone
  Tool = -> Cone001
FEATURE [Part::Fuse] Fusion112
  Base = -> Chamfer
  Tool = -> Fusion111
FEATURE [Part::Fuse] Fusion113
  Base = -> Cylinder079
  Tool = -> Cylinder080
FEATURE [Part::Cut] Cut045027
  Base = -> Fusion112
  Tool = -> Fusion113
FEATURE [Part::Cylinder] Cylinder081  label="Cylinder137"
  Angle = 360
  Height = 14.5
  Placement = pos=(-43.6,-2.4,-15) rot=(0,0,1;0rad)
  Radius = 0.8
FEATURE [Part::Cylinder] Cylinder082  label="Cylinder138"
  Angle = 360
  Height = 14.5
  Placement = pos=(-43.6,-13.8,-15) rot=(0,0,1;0rad)
  Radius = 0.8
FEATURE [Part::Box] Box044  label="Cube042"
  Height = 4
  Length = 12
  Placement = pos=(-50,-16.75,-14) rot=(0,0,1;0rad)
  Width = 26.75
FEATURE [Part::Chamfer] Chamfer001
  Base = -> Box044
  Edges = 1 edges r=7: [Edge3]
FEATURE [Part::Cone] Cone002
  Angle = 360
  Height = 1.5
  Placement = pos=(-43.6,-2.4,-10) rot=(0,0,1;0rad)
  Radius1 = 2.75
  Radius2 = 1.25
FEATURE [Part::Cone] Cone003
  Angle = 360
  Height = 1.5
  Placement = pos=(-43.6,-13.8,-10) rot=(0,0,1;0rad)
  Radius1 = 2.75
  Radius2 = 1.25
FEATURE [Part::Fuse] Fusion114
  Base = -> Cone002
  Tool = -> Cone003
FEATURE [Part::Fuse] Fusion115
  Base = -> Chamfer001
  Tool = -> Fusion114
FEATURE [Part::Fuse] Fusion116
  Base = -> Cylinder081
  Tool = -> Cylinder082
FEATURE [Part::Cut] Cut045028
  Base = -> Fusion115
  Tool = -> Fusion116
FEATURE [Part::Mirroring] Part__Mirroring005  label="Cut045028 (Mirror #6)"
  Base = (0,0,0)
  Normal = (1,0,0)
  Placement = pos=(27,0,0) rot=(0,0,1;0rad)
  Source = -> Cut045028
FEATURE [Part::Cut] Cut045029
  Base = -> Box010
  Tool = -> Fusion071
FEATURE [Part::Cut] Cut045030
  Base = -> Box011
  Tool = -> Fusion073
FEATURE [Part::MultiFuse] Fusion117
  Shapes = -> [Box015,Box016,Box017]
FEATURE [Part::Fuse] Fusion118
  Base = -> Fusion110
  Tool = -> Fusion117
FEATURE [Part::MultiFuse] Fusion119
  Shapes = -> [Fusion118,Cut045030,Cut045029]
FEATURE [Part::MultiFuse] Fusion120
  Shapes = -> [Fusion119,Part__Mirroring005,Cut045027]
FEATURE [Part::Cut] Cut045031
  Base = -> Fusion120
  Tool = -> Fusion057
FEATURE [Part::Cut] Cut045032
  Base = -> Cut045031
  Tool = -> Fusion058
FEATURE [Part::Cut] Cut045033
  Base = -> Cut045032
  Tool = -> Part__Mirroring003
FEATURE [Part::Cut] Cut045034
  Base = -> Cut045033
  Tool = -> Part__Mirroring004
FEATURE [Part::MultiFuse] Fusion121
  Shapes = -> [Cut045034,Box013,Box012]
FEATURE [Part::Chamfer] Chamfer002
  Base = -> Fusion121
  Edges = 1 edges r=25: [Edge244]
FEATURE [Part::Chamfer] Chamfer003
  Base = -> Fusion121
  Edges = 1 edges r=25: [Edge43]
FEATURE [Part::Chamfer] Chamfer004
  Base = -> Chamfer003
  Edges = 1 edges r=25: [Edge225]
FEATURE [Part::Chamfer] Chamfer005
  Base = -> Chamfer004
  Edges = 1 edges r=30: [Edge58]
FEATURE [Part::Chamfer] Chamfer006
  Base = -> Chamfer005
  Edges = 1 edges r=30: [Edge148]
FEATURE [Part::Fillet] Fillet
  Base = -> Chamfer006
  Edges = 1 edges r=2: [Edge233]
FEATURE [Part::Fillet] Fillet001
  Base = -> Fillet
  Edges = 1 edges r=2: [Edge6]
FEATURE [Part::Fillet] Fillet002
  Base = -> Fillet001
  Edges = 1 edges r=2: [Edge2]
FEATURE [Part::Fillet] Fillet003
  Base = -> Fillet002
  Edges = 1 edges r=2: [Edge357]
FEATURE [Part::Fillet] Fillet004
  Base = -> Fillet003
  Edges = 1 edges r=2: [Edge6]
FEATURE [Part::Fillet] Fillet005
  Base = -> Fillet004
  Edges = 1 edges r=2: [Edge2]
FEATURE [Part::Fillet] Fillet006
  Base = -> Fillet005
  Edges = 1 edges r=2: [Edge407]
FEATURE [Part::Fillet] Fillet007
  Base = -> Fillet006
  Edges = 1 edges r=2: [Edge2]
FEATURE [Part::Fillet] Fillet008
  Base = -> Fillet007
  Edges = 1 edges r=2: [Edge369]
FEATURE [Part::Fillet] Fillet009
  Base = -> Fillet008
  Edges = 1 edges r=2: [Edge2]
FEATURE [Part::Cylinder] Cylinder083  label="Cylinder139"
  Angle = 360
  Height = 28
  Placement = pos=(45,6,47) rot=(0.707107,0,0.707107;4.01426rad)
  Radius = 0.5
FEATURE [Part::Cylinder] Cylinder084  label="Cylinder140"
  Angle = 360
  Height = 28
  Placement = pos=(66,6,26) rot=(0.707107,0,0.707107;4.01426rad)
  Radius = 0.5
FEATURE [Part::Cut] Cut045035
  Base = -> Fillet009
  Tool = -> Cylinder083
FEATURE [Part::Cut] Cut045036
  Base = -> Cut045035
  Tool = -> Cylinder084
FEATURE [Part::Cylinder] Cylinder085  label="Cylinder141"
  Angle = 360
  Height = 28
  Placement = pos=(66,6,26) rot=(0.707107,0,0.707107;4.01426rad)
  Radius = 0.5
FEATURE [Part::Mirroring] Part__Mirroring006  label="Cylinder137 (Mirror #7)"
  Base = (0,0,0)
  Normal = (1,0,0)
  Placement = pos=(27,0,0) rot=(0,0,1;0rad)
  Source = -> Cylinder085
FEATURE [Part::Cylinder] Cylinder086  label="Cylinder142"
  Angle = 360
  Height = 28
  Placement = pos=(45,6,47) rot=(0.707107,0,0.707107;4.01426rad)
  Radius = 0.5
FEATURE [Part::Mirroring] Part__Mirroring007  label="Cylinder138 (Mirror #8)"
  Base = (0,0,0)
  Normal = (1,0,0)
  Placement = pos=(27,0,0) rot=(0,0,1;0rad)
  Source = -> Cylinder086
FEATURE [Part::Cut] Cut045037
  Base = -> Cut045036
  Tool = -> Part__Mirroring006
FEATURE [Part::Cut] Cut045038
  Base = -> Cut045037
  Tool = -> Part__Mirroring007
